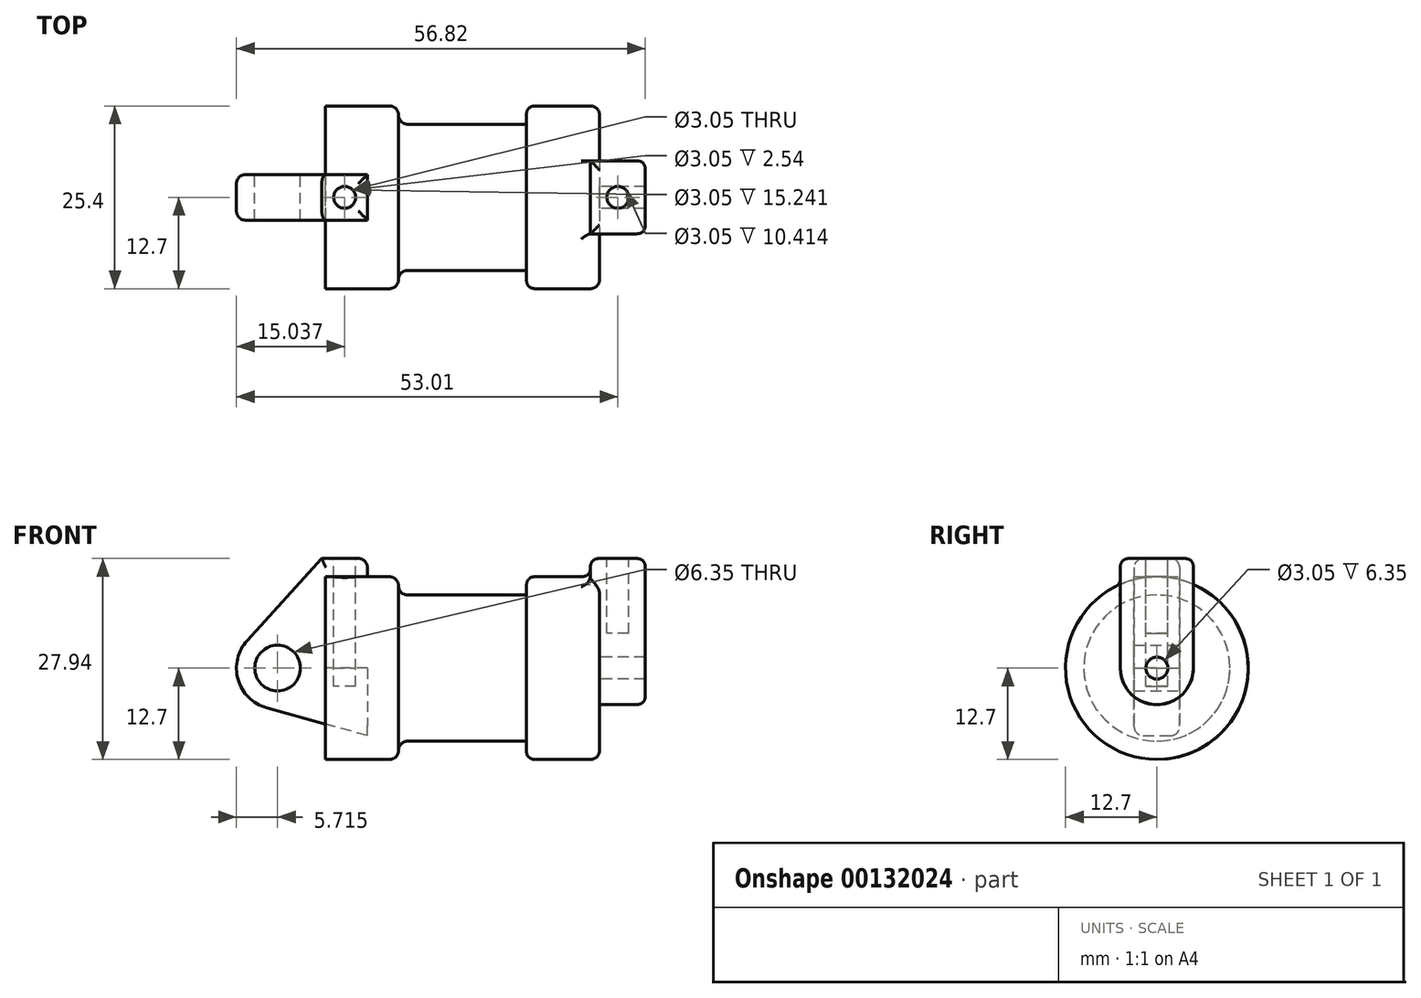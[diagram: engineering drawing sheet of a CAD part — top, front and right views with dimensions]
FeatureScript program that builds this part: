
annotation { "Feature Type Name" : "Feature", "Feature Type Description" : "" }
export const myFeature = defineFeature(function(context is Context, id is Id, definition is map)
    precondition{}
    {
        {
            var Q0;
            Q0=qCreatedBy(makeId("Front.planeOp"),FACE);
            var sketch = newSketch(context, id + "F0", { "sketchPlane" : qUnion([Q0])});
            skLineSegment(sketch, "E0", {"start": v(0, 0) * mm, "end": v(0, 12.7) * mm});
            skLineSegment(sketch, "E1", {"start": v(0, 12.7) * mm, "end": v(10.16, 12.7) * mm});
            skLineSegment(sketch, "E2", {"start": v(10.16, 12.7) * mm, "end": v(10.16, 10.16) * mm});
            skLineSegment(sketch, "E3", {"start": v(10.16, 10.16) * mm, "end": v(27.94, 10.16) * mm});
            skLineSegment(sketch, "E4", {"start": v(27.94, 10.16) * mm, "end": v(27.94, 12.7) * mm});
            skLineSegment(sketch, "E5", {"start": v(27.94, 12.7) * mm, "end": v(38.1, 12.7) * mm});
            skLineSegment(sketch, "E6", {"start": v(38.1, 12.7) * mm, "end": v(38.1, 0) * mm});
            skLineSegment(sketch, "E7", {"start": v(38.1, 0) * mm, "end": v(0, 0) * mm});
            skLineSegment(sketch, "E8", {"start": v(5.84, 15.24) * mm, "end": v(-0.5, 15.24) * mm});
            skLineSegment(sketch, "E9", {"start": v(-0.5, 15.24) * mm, "end": v(-10.88, 3.85) * mm});
            skLineSegment(sketch, "E10", {"start": v(0, 0) * mm, "end": v(-6.65, 0) * mm});
            skCircle(sketch, "E11", {"center": v(-6.65, 0) * mm, "radius": 5.72 * mm});
            skCircle(sketch, "E12", {"center": v(-6.65, 0) * mm, "radius": 3.18 * mm});
            skLineSegment(sketch, "E13", {"start": v(5.84, 15.24) * mm, "end": v(5.84, -9.4) * mm});
            skLineSegment(sketch, "E14", {"start": v(5.84, -9.4) * mm, "end": v(-8.18, -5.5) * mm});
            skSolve(sketch);
        }
        {
            var Q0;
            {var subQ0=sQuery(id+"F0.wireOp",EDGE,"E2");Q0=makeQuery(id+"F0.imprint","IMPRINT",FACE,{"disambiguationData":[TD([[makeQuery(id+"F0.imprint","IMPRINT",EDGE,{"derivedFrom":subQ0}),-1.0]])]});}
            var Q1;
            {var subQ0=sQuery(id+"F0.wireOp",EDGE,"E0");Q1=makeQuery(id+"F0.imprint","IMPRINT",FACE,{"disambiguationData":[TD([[makeQuery(id+"F0.imprint","IMPRINT",EDGE,{"derivedFrom":subQ0}),-1.0]])]});}
            var Q2;
            Q2=sQuery(id+"F0.wireOp",EDGE,"E7");
            revolve(context, id + "F1", {"entities" : qUnion([Q0, Q1]), "axis" : qUnion([Q2]), "revolveType" : RevolveType.FULL});
        }
        {
            var Q0;
            {var subQ3=sQuery(id+"F0.wireOp",EDGE,"E0");Q0=makeQuery(id+"F0.imprint","IMPRINT",FACE,{"disambiguationData":[TD([[makeQuery(id+"F0.imprint","IMPRINT",EDGE,{"derivedFrom":subQ3}),1.0]])]});}
            var Q1;
            {var subQ4=sQuery(id+"F0.wireOp",EDGE,"E12");Q1=makeQuery(id+"F0.imprint","IMPRINT",FACE,{"disambiguationData":[TD([[makeQuery(id+"F0.imprint","IMPRINT",EDGE,{"derivedFrom":subQ4}),-1.0]])]});}
            var Q2;
            {var subQ0=sQuery(id+"F0.wireOp",EDGE,"E14");Q2=makeQuery(id+"F0.imprint","IMPRINT",FACE,{"disambiguationData":[TD([[makeQuery(id+"F0.imprint","IMPRINT",EDGE,{"derivedFrom":subQ0}),-1.0]])]});}
            extrude(context, id + "F2", {"entities" : qUnion([Q0, Q1, Q2]), "endBound" : BoundingType.SYMMETRIC, "depth" : 6.35 * mm});
        }
        {
            var Q0;
            Q0=makeQuery(id+"F1.opRevolve","SWEPT_FACE",FACE,{"disambiguationData":[OSD([sQuery(id+"F0.wireOp",EDGE,"E6")])]});
            var sketch = newSketch(context, id + "F3", { "sketchPlane" : qUnion([Q0])});
            skCircle(sketch, "E15", {"center": v(0, 0) * mm, "radius": 1.52 * mm});
            skArc(sketch, "E16", {"start": v(-5.08, 0) * mm, "mid": v(0, -5.08) * mm, "end": v(5.08, 0) * mm});
            skLineSegment(sketch, "E17.top", {"start": v(5.08, 15.24) * mm, "end": v(-5.08, 15.24) * mm});
            skLineSegment(sketch, "E17.left", {"start": v(5.08, 0) * mm, "end": v(5.08, 15.24) * mm});
            skLineSegment(sketch, "E17.right", {"start": v(-5.08, 0) * mm, "end": v(-5.08, 15.24) * mm});
            skSolve(sketch);
        }
        {
            var Q0;
            Q0=makeQuery(id+"F3.imprint","IMPRINT",FACE,{"disambiguationData":[TD([[makeQuery(id+"F3.imprint","IMPRINT",EDGE,{"derivedFrom":sQuery(id+"F3.wireOp",EDGE,"E15")}),-1.0]])]});
            var Q1;
            {var subQ0=sQuery(id+"F3.wireOp",EDGE,"E17.top");Q1=makeQuery(id+"F3.imprint","IMPRINT",FACE,{"disambiguationData":[TD([[makeQuery(id+"F3.imprint","IMPRINT",EDGE,{"derivedFrom":subQ0}),1.0]])]});}
            extrude(context, id + "F4", {"entities" : qUnion([Q0, Q1]), "operationType" : NewBodyOperationType.ADD, "depth" : 6.35 * mm, "hasSecondDirection" : true, "secondDirectionOppositeDirection" : true, "secondDirectionDepth" : 1.27 * mm});
        }
        {
            var Q0;
            Q0=makeQuery(id+"F2.opExtrude","SWEPT_FACE",FACE,{"disambiguationData":[OSD([sQuery(id+"F0.wireOp",EDGE,"E8")])]});
            var sketch = newSketch(context, id + "F5", { "sketchPlane" : qUnion([Q0])});
            skCircle(sketch, "E18", {"center": v(2.67, 0) * mm, "radius": 1.52 * mm});
            skSolve(sketch);
        }
        {
            var Q0;
            Q0=makeQuery(id+"F5.imprint","IMPRINT",FACE,{"disambiguationData":[TD([[makeQuery(id+"F5.imprint","IMPRINT",EDGE,{"derivedFrom":sQuery(id+"F5.wireOp",EDGE,"E18")}),1.0]])]});
            var Q1;
            Q1=sQuery(id+"F5.wireOp",EDGE,"E18");
            extrude(context, id + "F6", {"entities" : qUnion([Q0]), "operationType" : NewBodyOperationType.REMOVE, "surfaceEntities" : qUnion([Q1]), "oppositeDirection" : true, "depth" : 17.78 * mm});
        }
        {
            var Q0;
            Q0=makeQuery(id+"F4.opExtrude","SWEPT_FACE",FACE,{"disambiguationData":[OSD([sQuery(id+"F3.wireOp",EDGE,"E17.top")])]});
            var sketch = newSketch(context, id + "F7", { "sketchPlane" : qUnion([Q0])});
            skCircle(sketch, "E19", {"center": v(40.64, 0) * mm, "radius": 1.52 * mm});
            skSolve(sketch);
        }
        {
            var Q0;
            Q0=makeQuery(id+"F7.imprint","IMPRINT",FACE,{"disambiguationData":[TD([[makeQuery(id+"F7.imprint","IMPRINT",EDGE,{"derivedFrom":sQuery(id+"F7.wireOp",EDGE,"E19")}),1.0]])]});
            extrude(context, id + "F8", {"entities" : qUnion([Q0]), "operationType" : NewBodyOperationType.REMOVE, "oppositeDirection" : true, "depth" : 10.4 * mm});
        }
        {
            var Q0;
            Q0=makeQuery(id+"F4.opExtrude","CAP_EDGE",EDGE,{"disambiguationData":[OSD([sQuery(id+"F3.wireOp",EDGE,"E17.right")])],"isStart":false});
            fillet(context, id + "F9", {"entities" : qUnion([Q0]), "radius" : 1.27 * mm, "tangentPropagation" : true, "rho" : 0.5, "crossSection" : FilletCrossSection.CONIC, "allowEdgeOverflow" : false});
        }
        {
            var Q0;
            Q0=makeQuery(id+"F4.opExtrude","SWEPT_EDGE",EDGE,{"disambiguationData":[OSD([sQuery(id+"F3.wireOp",EDGE,"E17.top"),sQuery(id+"F3.wireOp",EDGE,"E17.right")])]});
            var Q1;
            Q1=makeQuery(id+"F4.opExtrude","CAP_EDGE",EDGE,{"disambiguationData":[OSD([sQuery(id+"F3.wireOp",EDGE,"E17.top")])],"isStart":true});
            var Q2;
            Q2=makeQuery(id+"F4.boolean.opBoolean","INTERSECT",EDGE,{"derivedFrom":[makeQuery(id+"F1.opRevolve","SWEPT_FACE",FACE,{"disambiguationData":[OSD([sQuery(id+"F0.wireOp",EDGE,"E5")])]}),makeQuery(id+"F4.opExtrude","CAP_FACE",FACE,{"disambiguationData":[OSD([sQuery(id+"F3.wireOp",EDGE,"E15"),sQuery(id+"F3.wireOp",EDGE,"E16"),sQuery(id+"F3.wireOp",EDGE,"E17.top"),sQuery(id+"F3.wireOp",EDGE,"E17.left"),sQuery(id+"F3.wireOp",EDGE,"E17.right")])],"isStart":true})]});
            var Q3;
            Q3=makeQuery(id+"F1.opRevolve","SWEPT_EDGE",EDGE,{"disambiguationData":[OSD([sQuery(id+"F0.wireOp",EDGE,"E4"),sQuery(id+"F0.wireOp",EDGE,"E5")])]});
            var Q4;
            Q4=makeQuery(id+"F4.boolean.opBoolean","INTERSECT",EDGE,{"derivedFrom":[makeQuery(id+"F1.opRevolve","SWEPT_FACE",FACE,{"disambiguationData":[OSD([sQuery(id+"F0.wireOp",EDGE,"E5")])]}),makeQuery(id+"F4.opExtrude","SWEPT_FACE",FACE,{"disambiguationData":[OSD([sQuery(id+"F3.wireOp",EDGE,"E17.right")])]})]});
            fillet(context, id + "F10", {"entities" : qUnion([Q0, Q1, Q2, Q3, Q4]), "radius" : 1.27 * mm, "tangentPropagation" : true, "rho" : 0.5, "crossSection" : FilletCrossSection.CONIC, "allowEdgeOverflow" : false});
        }
        {
            var Q0;
            Q0=makeQuery(id+"F1.opRevolve","SWEPT_EDGE",EDGE,{"disambiguationData":[OSD([sQuery(id+"F0.wireOp",EDGE,"E5"),sQuery(id+"F0.wireOp",EDGE,"E6")])]});
            fillet(context, id + "F11", {"entities" : qUnion([Q0]), "radius" : 1.27 * mm, "tangentPropagation" : true, "allowEdgeOverflow" : false});
        }
        {
            var Q0;
            Q0=makeQuery(id+"F1.opRevolve","SWEPT_EDGE",EDGE,{"disambiguationData":[OSD([sQuery(id+"F0.wireOp",EDGE,"E2"),sQuery(id+"F0.wireOp",EDGE,"E3")])]});
            var Q1;
            Q1=makeQuery(id+"F1.opRevolve","SWEPT_EDGE",EDGE,{"disambiguationData":[OSD([sQuery(id+"F0.wireOp",EDGE,"E1"),sQuery(id+"F0.wireOp",EDGE,"E2")])]});
            fillet(context, id + "F12", {"entities" : qUnion([Q0, Q1]), "radius" : 1.27 * mm, "tangentPropagation" : true, "allowEdgeOverflow" : false});
        }
        {
            var Q0;
            Q0=makeQuery(id+"F2.opExtrude","CAP_EDGE",EDGE,{"disambiguationData":[OSD([sQuery(id+"F0.wireOp",EDGE,"E9")])],"isStart":false});
            var Q1;
            Q1=makeQuery(id+"F2.opExtrude","CAP_EDGE",EDGE,{"disambiguationData":[OSD([sQuery(id+"F0.wireOp",EDGE,"E11")])],"isStart":false});
            var Q2;
            Q2=makeQuery(id+"F2.opExtrude","CAP_EDGE",EDGE,{"disambiguationData":[OSD([sQuery(id+"F0.wireOp",EDGE,"E8")])],"isStart":false});
            var Q3;
            Q3=makeQuery(id+"F2.opExtrude","SWEPT_EDGE",EDGE,{"disambiguationData":[OSD([sQuery(id+"F0.wireOp",EDGE,"E8"),sQuery(id+"F0.wireOp",EDGE,"E13")])]});
            var Q4;
            Q4=makeQuery(id+"F2.opExtrude","CAP_EDGE",EDGE,{"disambiguationData":[OSD([sQuery(id+"F0.wireOp",EDGE,"E8")])],"isStart":true});
            var Q5;
            Q5=makeQuery(id+"F2.opExtrude","CAP_EDGE",EDGE,{"disambiguationData":[OSD([sQuery(id+"F0.wireOp",EDGE,"E9")])],"isStart":true});
            fillet(context, id + "F13", {"entities" : qUnion([Q0, Q1, Q2, Q3, Q4, Q5]), "radius" : 1.27 * mm, "tangentPropagation" : true, "allowEdgeOverflow" : false});
        }
    });
